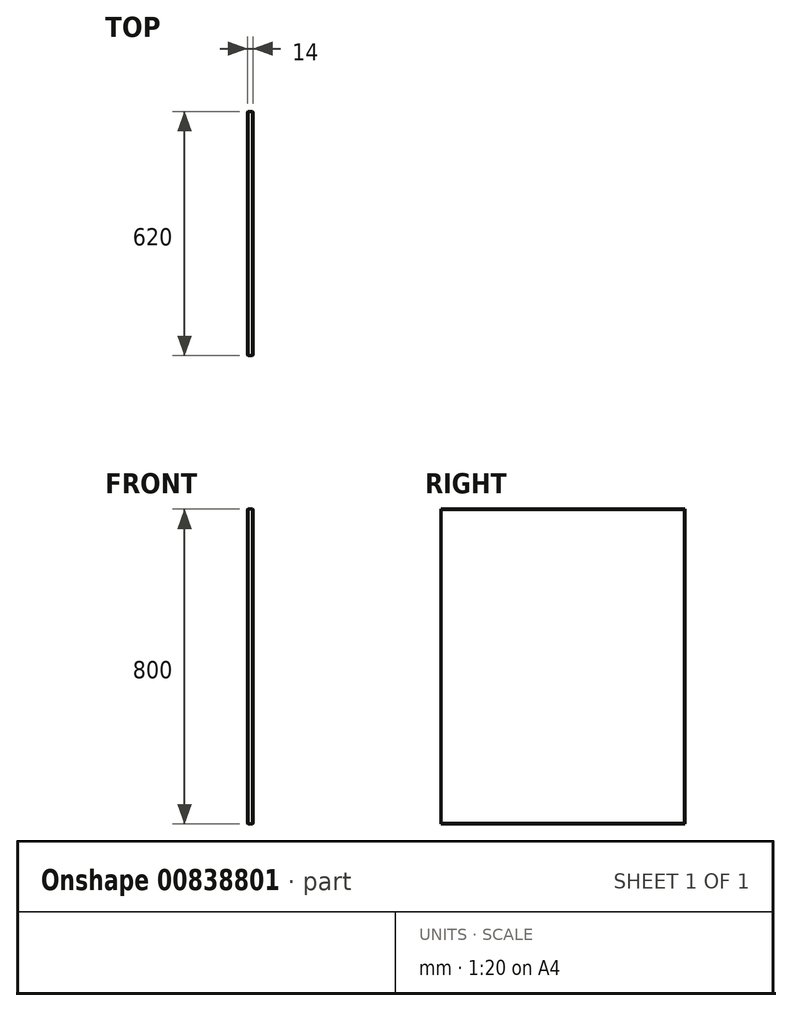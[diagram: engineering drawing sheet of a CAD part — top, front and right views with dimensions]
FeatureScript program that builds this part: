
annotation { "Feature Type Name" : "Feature", "Feature Type Description" : "" }
export const myFeature = defineFeature(function(context is Context, id is Id, definition is map)
    precondition{}
    {
        {
            var Q0;
            Q0=qCreatedBy(makeId("Right.planeOp"),FACE);
            var sketch = newSketch(context, id + "F0", { "sketchPlane" : qUnion([Q0])});
            skLineSegment(sketch, "E0.bottom", {"start": v(0, 0) * mm, "end": v(-50.65, 0) * mm});
            skLineSegment(sketch, "E0.top", {"start": v(0, 38.28) * mm, "end": v(-50.65, 38.28) * mm});
            skLineSegment(sketch, "E0.left", {"start": v(0, 0) * mm, "end": v(0, 38.28) * mm});
            skLineSegment(sketch, "E0.right", {"start": v(-50.65, 0) * mm, "end": v(-50.65, 38.28) * mm});
            skSolve(sketch);
        }
        {
            var Q0;
            Q0=makeQuery(id+"F0.imprint","IMPRINT",FACE,{"disambiguationData":[TD([[makeQuery(id+"F0.imprint","IMPRINT",EDGE,{"derivedFrom":sQuery(id+"F0.wireOp",EDGE,"E0.bottom")}),-1.0]])]});
            extrude(context, id + "F1", {"entities" : qUnion([Q0]), "oppositeDirection" : true, "depth" : 14 * mm, "offsetDistance" : 25.4 * mm});
        }
        {
            var Q0;
            Q0=makeQuery(id+"F1.opExtrude","SWEPT_FACE",FACE,{"disambiguationData":[OSD([sQuery(id+"F0.wireOp",EDGE,"E0.bottom")])]});
            extrude(context, id + "F2", {"entities" : qUnion([Q0]), "operationType" : NewBodyOperationType.ADD, "oppositeDirection" : true, "depth" : 2200 * mm, "offsetDistance" : 25.4 * mm});
        }
        {
            var Q0;
            {var subQ0=sQuery(id+"F0.wireOp",EDGE,"E0.left");Q0=makeQuery(id+"F2.boolean.opBoolean","MERGE",FACE,{"derivedFrom":[makeQuery(id+"F1.opExtrude","SWEPT_FACE",FACE,{"disambiguationData":[OSD([subQ0])]}),makeQuery(id+"F2.opExtrude","SWEPT_FACE",FACE,{"disambiguationData":[OSD([sQuery(id+"F0.wireOp",EDGE,"E0.bottom"),subQ0])]})]});}
            extrude(context, id + "F3", {"entities" : qUnion([Q0]), "operationType" : NewBodyOperationType.ADD, "oppositeDirection" : true, "depth" : 620 * mm, "offsetDistance" : 25 * mm});
        }
        {
            var Q0;
            {var subQ0=sQuery(id+"F0.wireOp",EDGE,"E0.left");var subQ1=sQuery(id+"F0.wireOp",EDGE,"E0.bottom");Q0=makeQuery(id+"F3.boolean.opBoolean","MERGE",FACE,{"derivedFrom":[makeQuery(id+"F2.opExtrude","CAP_FACE",FACE,{"disambiguationData":[OSD([subQ1])],"isStart":false}),makeQuery(id+"F3.opExtrude","SWEPT_FACE",FACE,{"disambiguationData":[OSD([subQ1,subQ0]),TDD([makeQuery(id+"F2.opExtrude","CAP_EDGE",EDGE,{"disambiguationData":[OSD([subQ1,subQ0])],"isStart":false})])]})]});}
            extrude(context, id + "F4", {"entities" : qUnion([Q0]), "operationType" : NewBodyOperationType.REMOVE, "oppositeDirection" : true, "depth" : 400 * mm, "offsetDistance" : 25 * mm});
        }
        {
            var Q0;
            Q0=makeQuery(id+"F4.boolean.opBoolean","COPY",FACE,{"derivedFrom":makeQuery(id+"F4.opExtrude","CAP_FACE",FACE,{"disambiguationData":[OSD([sQuery(id+"F0.wireOp",EDGE,"E0.bottom"),sQuery(id+"F0.wireOp",EDGE,"E0.left")])],"isStart":false})});
            extrude(context, id + "F5", {"entities" : qUnion([Q0]), "operationType" : NewBodyOperationType.REMOVE, "oppositeDirection" : true, "depth" : 1000 * mm, "offsetDistance" : 25 * mm});
        }
        {
            var Q0;
            {var subQ0=sQuery(id+"F0.wireOp",EDGE,"E0.left");var subQ1=sQuery(id+"F0.wireOp",EDGE,"E0.bottom");Q0=makeQuery(id+"F3.boolean.opBoolean","MERGE",FACE,{"derivedFrom":[makeQuery(id+"F2.boolean.opBoolean","MERGE",FACE,{"derivedFrom":[makeQuery(id+"F1.opExtrude","CAP_FACE",FACE,{"disambiguationData":[OSD([subQ1,sQuery(id+"F0.wireOp",EDGE,"E0.top"),subQ0,sQuery(id+"F0.wireOp",EDGE,"E0.right")])],"isStart":true}),makeQuery(id+"F2.opExtrude","SWEPT_FACE",FACE,{"disambiguationData":[OSD([subQ1]),TDD([makeQuery(id+"F1.opExtrude","CAP_EDGE",EDGE,{"disambiguationData":[OSD([subQ1])],"isStart":true})])]})]}),makeQuery(id+"F3.opExtrude","SWEPT_FACE",FACE,{"disambiguationData":[OSD([subQ1,subQ0]),TDD([makeQuery(id+"F2.boolean.opBoolean","MERGE",EDGE,{"derivedFrom":[makeQuery(id+"F1.opExtrude","CAP_EDGE",EDGE,{"disambiguationData":[OSD([subQ0])],"isStart":true}),makeQuery(id+"F2.opExtrude","SWEPT_EDGE",EDGE,{"disambiguationData":[OSD([subQ1,subQ0]),TDD([makeQuery(id+"F1.opExtrude","CAP_VERTEX",VERTEX,{"disambiguationData":[OSD([subQ1,subQ0])],"isStart":true})])]})]})])]})]});}
            var Q1;
            {var subQ0=sQuery(id+"F0.wireOp",EDGE,"E0.left");var subQ1=sQuery(id+"F0.wireOp",EDGE,"E0.bottom");Q1=makeQuery(id+"F3.boolean.opBoolean","MERGE",FACE,{"derivedFrom":[makeQuery(id+"F2.boolean.opBoolean","MERGE",FACE,{"derivedFrom":[makeQuery(id+"F1.opExtrude","CAP_FACE",FACE,{"disambiguationData":[OSD([subQ1,sQuery(id+"F0.wireOp",EDGE,"E0.top"),subQ0,sQuery(id+"F0.wireOp",EDGE,"E0.right")])],"isStart":false}),makeQuery(id+"F2.opExtrude","SWEPT_FACE",FACE,{"disambiguationData":[OSD([subQ1]),TDD([makeQuery(id+"F1.opExtrude","CAP_EDGE",EDGE,{"disambiguationData":[OSD([subQ1])],"isStart":false})])]})]}),makeQuery(id+"F3.opExtrude","SWEPT_FACE",FACE,{"disambiguationData":[OSD([subQ1,subQ0]),TDD([makeQuery(id+"F2.boolean.opBoolean","MERGE",EDGE,{"derivedFrom":[makeQuery(id+"F1.opExtrude","CAP_EDGE",EDGE,{"disambiguationData":[OSD([subQ0])],"isStart":false}),makeQuery(id+"F2.opExtrude","SWEPT_EDGE",EDGE,{"disambiguationData":[OSD([subQ1,subQ0]),TDD([makeQuery(id+"F1.opExtrude","CAP_VERTEX",VERTEX,{"disambiguationData":[OSD([subQ1,subQ0])],"isStart":false})])]})]})])]})]});}
            chamfer(context, id + "F6", {"entities" : qUnion([Q0, Q1]), "width" : 1 * mm, "tangentPropagation" : true});
        }
    });
